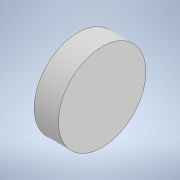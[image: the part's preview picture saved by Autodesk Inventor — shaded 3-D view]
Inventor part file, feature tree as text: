
AUTODESK INVENTOR PART (.ipt)
format: ipt  version: 2022 (Build 260153000, 153)  size: 92,672 bytes
history: native  units: mm
features: other x1, extrude x1, sketch x1
ambient origin geometry x8: Origin, YZ Plane, XZ Plane, XY Plane, X Axis, Y Axis, Z Axis, Center Point
bodies: Body1 (feature_tree)
feature tree (3):
  other  "솔리드1"
  extrude  "돌출1"  Depth=9.0mm
  sketch  "스케치3"
